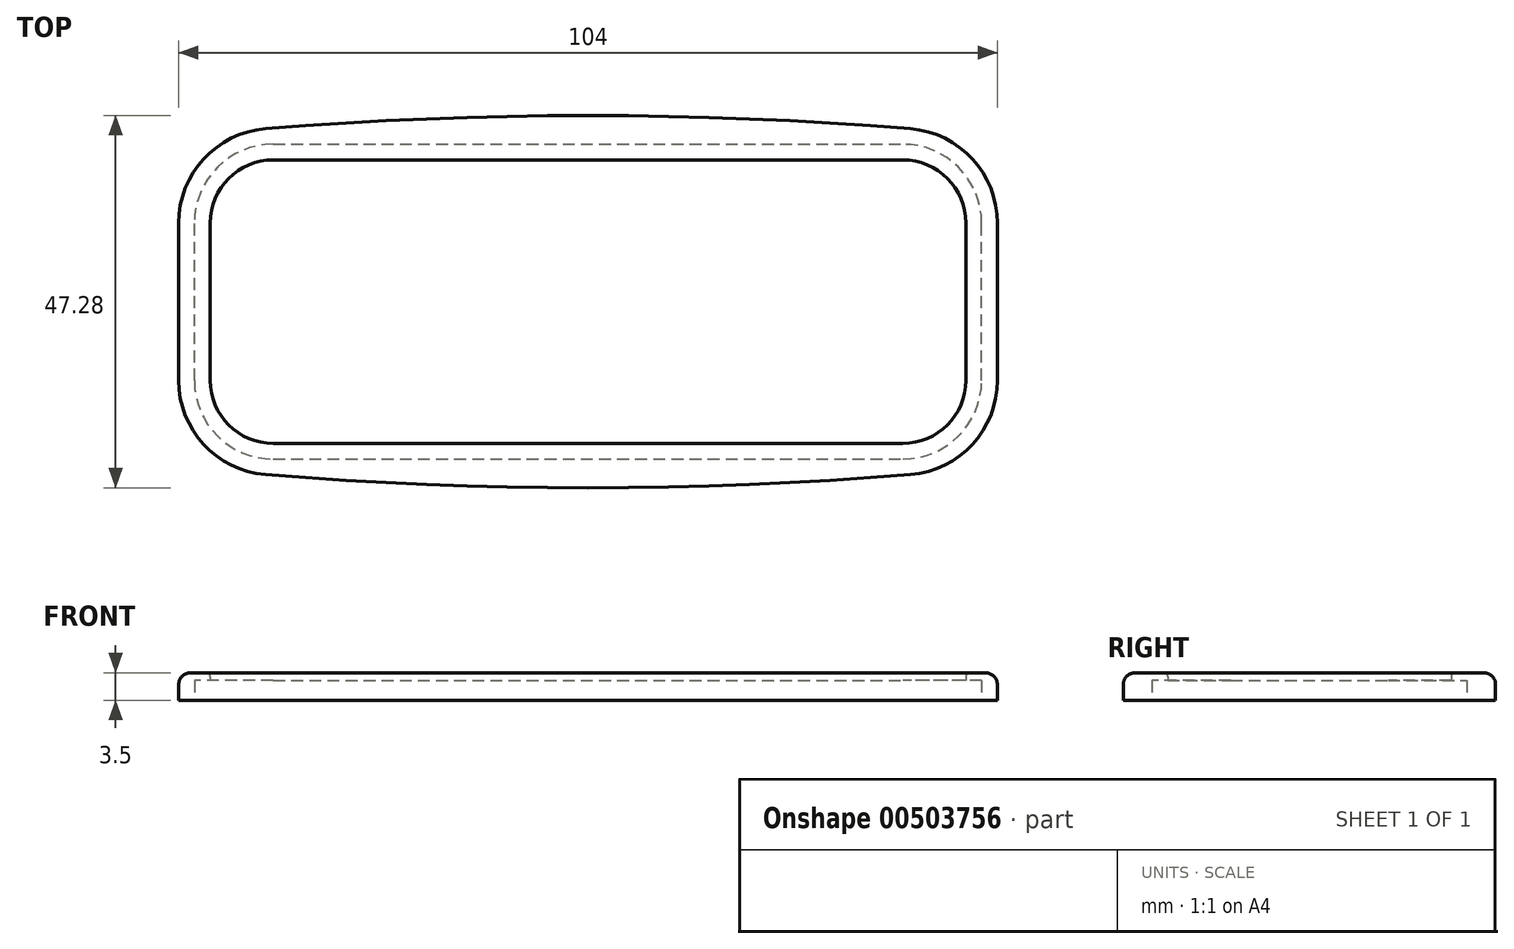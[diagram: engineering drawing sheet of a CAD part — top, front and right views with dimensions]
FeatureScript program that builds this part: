
annotation { "Feature Type Name" : "Feature", "Feature Type Description" : "" }
export const myFeature = defineFeature(function(context is Context, id is Id, definition is map)
    precondition{}
    {
        {
            var Q0;
            Q0=qCreatedBy(makeId("Top.planeOp"),FACE);
            var sketch = newSketch(context, id + "F0", { "sketchPlane" : qUnion([Q0])});
            skLineSegment(sketch, "E0.bottom", {"start": v(10, 0) * mm, "end": v(90, 0) * mm});
            skLineSegment(sketch, "E0.top", {"start": v(10, 40) * mm, "end": v(90, 40) * mm});
            skLineSegment(sketch, "E0.left", {"start": v(0, 10) * mm, "end": v(0, 30) * mm});
            skLineSegment(sketch, "E0.right", {"start": v(100, 10) * mm, "end": v(100, 30) * mm});
            skPoint(sketch, "E1.visualSharp", {"position": v(0, 40) * mm});
            skArc(sketch, "E1.filletArc", {"start": v(10, 40) * mm, "mid": v(2.93, 37.07) * mm, "end": v(0, 30) * mm});
            skPoint(sketch, "E2.visualSharp", {"position": v(100, 40) * mm});
            skArc(sketch, "E2.filletArc", {"start": v(100, 30) * mm, "mid": v(97.07, 37.07) * mm, "end": v(90, 40) * mm});
            skPoint(sketch, "E3.visualSharp", {"position": v(100, 0) * mm});
            skArc(sketch, "E3.filletArc", {"start": v(90, 0) * mm, "mid": v(97.07, 2.93) * mm, "end": v(100, 10) * mm});
            skPoint(sketch, "E4.visualSharp", {"position": v(0, 0) * mm});
            skArc(sketch, "E4.filletArc", {"start": v(0, 10) * mm, "mid": v(2.93, 2.93) * mm, "end": v(10, 0) * mm});
            skSolve(sketch);
        }
        {
            var Q0;
            Q0 = qSketchRegion(id + "F0", true);
            extrude(context, id + "F1", {"entities" : qUnion([Q0]), "depth" : 2.5 * mm, "offsetDistance" : 25 * mm});
        }
        {
            var Q0;
            Q0=makeQuery(id+"F1.opExtrude","CAP_FACE",FACE,{"disambiguationData":[OSD([sQuery(id+"F0.wireOp",EDGE,"E0.bottom"),sQuery(id+"F0.wireOp",EDGE,"E0.top"),sQuery(id+"F0.wireOp",EDGE,"E0.left"),sQuery(id+"F0.wireOp",EDGE,"E0.right")])],"isStart":false});
            var sketch = newSketch(context, id + "F2", { "sketchPlane" : qUnion([Q0])});
            skText(sketch, "E5", { "text": "xxxx & xxxx", "fontName": "NotoSerif-BoldItalic.ttf"});
            skText(sketch, "E6", { "text": "Xxxxxxx", "fontName": "NotoSerif-BoldItalic.ttf"});
            const initialGuessF2  = {"E5": [0.01966, 0.027, 1, 0, 0.007], "E6": [0.00968, 0.006, 1, 0, 0.013]};
            skSetInitialGuess(sketch, initialGuessF2);
            skSolve(sketch);
        }
        {
            var Q0;
            Q0 = qSketchRegion(id + "F2", true);
            extrude(context, id + "F3", {"entities" : qUnion([Q0]), "operationType" : NewBodyOperationType.REMOVE, "oppositeDirection" : true, "depth" : .5 * mm});
        }
        {
            var Q0;
            Q0=qCreatedBy(makeId("Top.planeOp"),FACE);
            var sketch = newSketch(context, id + "F4", { "sketchPlane" : qUnion([Q0])});
            skArc(sketch, "E7.0", {"start": v(10, 38) * mm, "mid": v(4.34, 35.66) * mm, "end": v(2, 30) * mm});
            skLineSegment(sketch, "E7.1", {"start": v(2, 10) * mm, "end": v(2, 30) * mm});
            skLineSegment(sketch, "E7.2", {"start": v(10, 38) * mm, "end": v(90, 38) * mm});
            skArc(sketch, "E7.3", {"start": v(2, 10) * mm, "mid": v(4.34, 4.34) * mm, "end": v(10, 2) * mm});
            skArc(sketch, "E7.4", {"start": v(98, 30) * mm, "mid": v(95.66, 35.66) * mm, "end": v(90, 38) * mm});
            skLineSegment(sketch, "E7.5", {"start": v(98, 10) * mm, "end": v(98, 30) * mm});
            skArc(sketch, "E7.6", {"start": v(90, 2) * mm, "mid": v(95.66, 4.34) * mm, "end": v(98, 10) * mm});
            skLineSegment(sketch, "E7.7", {"start": v(10, 2) * mm, "end": v(90, 2) * mm});
            skArc(sketch, "E8.0", {"start": v(9.02, 41.96) * mm, "mid": v(1.17, 38.13) * mm, "end": v(-2, 30) * mm});
            skArc(sketch, "E9.0", {"start": v(102, 30) * mm, "mid": v(98.83, 38.13) * mm, "end": v(90.98, 41.96) * mm});
            skArc(sketch, "E10", {"start": v(90.98, 41.96) * mm, "mid": v(50, 43.64) * mm, "end": v(9.02, 41.96) * mm});
            skArc(sketch, "E11.0", {"start": v(90.98, -1.96) * mm, "mid": v(98.83, 1.87) * mm, "end": v(102, 10) * mm});
            skArc(sketch, "E12.0", {"start": v(-2, 10) * mm, "mid": v(1.17, 1.87) * mm, "end": v(9.02, -1.96) * mm});
            skArc(sketch, "E13", {"start": v(9.02, -1.96) * mm, "mid": v(50, -3.64) * mm, "end": v(90.98, -1.96) * mm});
            skLineSegment(sketch, "E14", {"start": v(-2, 10) * mm, "end": v(-2, 30) * mm});
            skLineSegment(sketch, "E15", {"start": v(102, 10) * mm, "end": v(102, 30) * mm});
            skSolve(sketch);
        }
        {
            var Q0;
            Q0=makeQuery(id+"F4.imprint","IMPRINT",FACE,{"disambiguationData":[TD([[makeQuery(id+"F4.imprint","IMPRINT",EDGE,{"derivedFrom":sQuery(id+"F4.wireOp",EDGE,"E7.0")}),-1.0]])]});
            extrude(context, id + "F5", {"entities" : qUnion([Q0]), "depth" : 3.5 * mm, "offsetDistance" : 25 * mm});
        }
        {
            var Q0;
            Q0=makeQuery(id+"F0.imprint","IMPRINT",FACE,{"disambiguationData":[TD([[makeQuery(id+"F0.imprint","IMPRINT",EDGE,{"derivedFrom":sQuery(id+"F0.wireOp",EDGE,"E0.bottom")}),1.0]])]});
            extrude(context, id + "F6", {"entities" : qUnion([Q0]), "operationType" : NewBodyOperationType.REMOVE, "depth" : 2.5 * mm, "offsetDistance" : 25 * mm});
        }
        {
            var Q0;
            Q0=makeQuery(id+"F5.opExtrude","CAP_EDGE",EDGE,{"disambiguationData":[OSD([sQuery(id+"F4.wireOp",EDGE,"E13")])],"isStart":false});
            fillet(context, id + "F7", {"entities" : qUnion([Q0]), "radius" : 1.5 * mm, "tangentPropagation" : true, "allowEdgeOverflow" : false});
        }
        {
            var Q0;
            Q0=makeQuery(id+"F5.opExtrude","CAP_EDGE",EDGE,{"disambiguationData":[OSD([sQuery(id+"F4.wireOp",EDGE,"E7.1")])],"isStart":false});
            fillet(context, id + "F8", {"entities" : qUnion([Q0]), "radius" : .5 * mm, "tangentPropagation" : true, "allowEdgeOverflow" : false});
        }
    });
